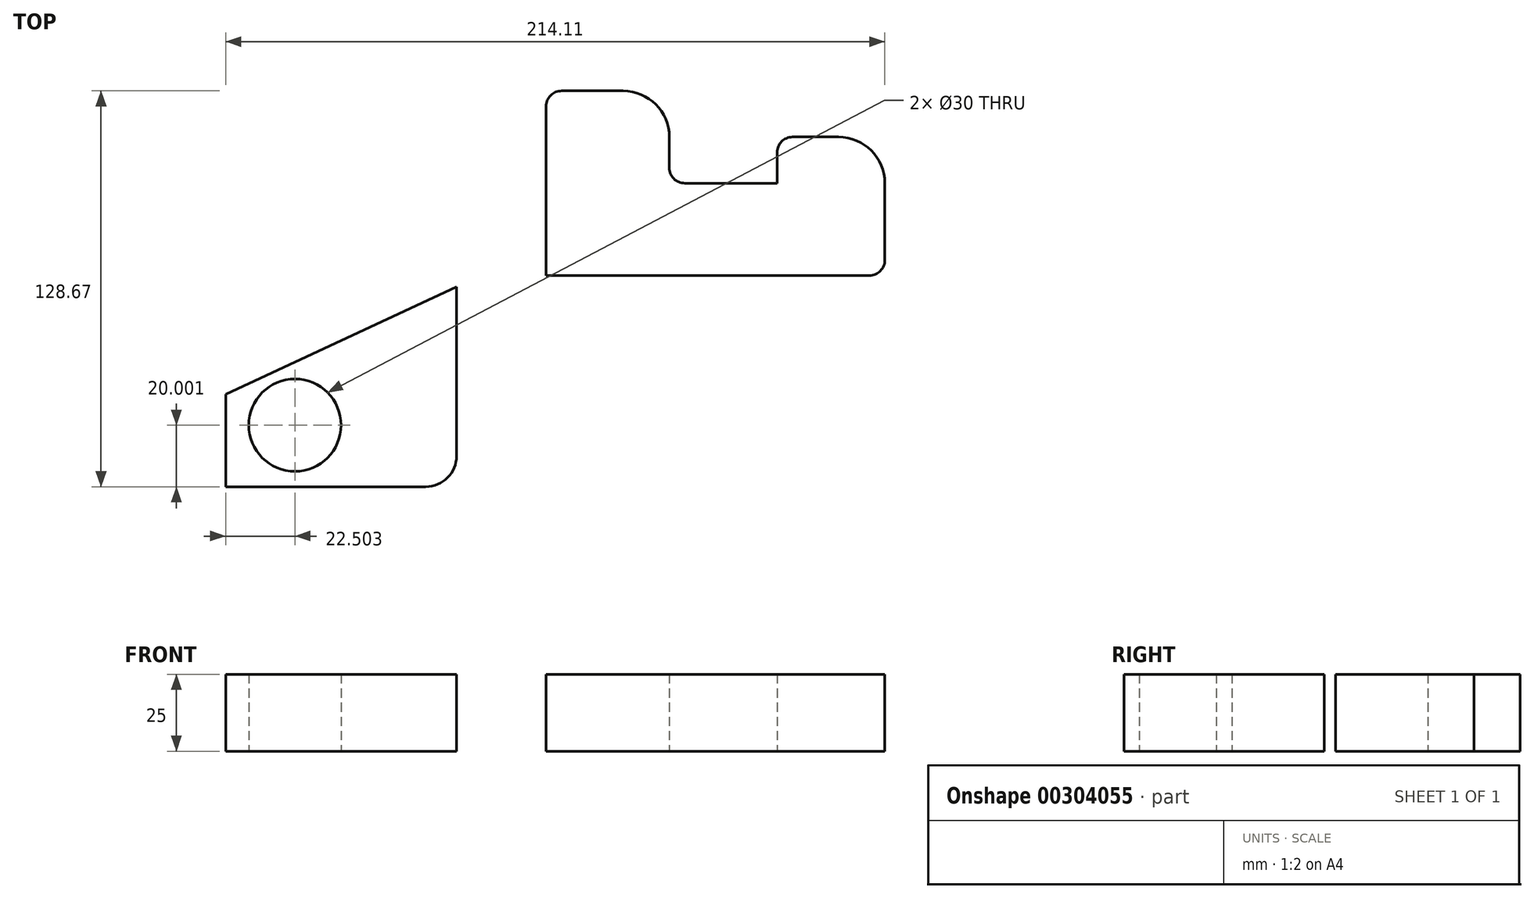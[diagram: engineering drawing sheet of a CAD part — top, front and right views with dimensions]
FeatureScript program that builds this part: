
annotation { "Feature Type Name" : "Feature", "Feature Type Description" : "" }
export const myFeature = defineFeature(function(context is Context, id is Id, definition is map)
    precondition{}
    {
        {
            var Q0;
            Q0=qCreatedBy(makeId("Top.planeOp"),FACE);
            var sketch = newSketch(context, id + "F0", { "sketchPlane" : qUnion([Q0])});
            skLineSegment(sketch, "E0", {"start": v(-72.12, -25.71) * mm, "end": v(32.88, -25.71) * mm});
            skLineSegment(sketch, "E1", {"start": v(37.88, -20.71) * mm, "end": v(37.88, 4.29) * mm});
            skPoint(sketch, "E2.visualSharp", {"position": v(37.88, -25.71) * mm});
            skArc(sketch, "E2.filletArc", {"start": v(32.88, -25.71) * mm, "mid": v(36.41, -24.25) * mm, "end": v(37.88, -20.71) * mm});
            skLineSegment(sketch, "E3", {"start": v(22.88, 19.29) * mm, "end": v(7.88, 19.29) * mm});
            skPoint(sketch, "E4.visualSharp", {"position": v(37.88, 19.29) * mm});
            skArc(sketch, "E4.filletArc", {"start": v(37.88, 4.29) * mm, "mid": v(33.48, 14.9) * mm, "end": v(22.88, 19.29) * mm});
            skLineSegment(sketch, "E5", {"start": v(2.88, 14.29) * mm, "end": v(2.88, 4.29) * mm});
            skPoint(sketch, "E6.visualSharp", {"position": v(2.88, 19.29) * mm});
            skArc(sketch, "E6.filletArc", {"start": v(7.88, 19.29) * mm, "mid": v(4.34, 17.82) * mm, "end": v(2.88, 14.29) * mm});
            skLineSegment(sketch, "E7", {"start": v(2.88, 4.29) * mm, "end": v(-27.12, 4.29) * mm});
            skLineSegment(sketch, "E8", {"start": v(-32.12, 9.29) * mm, "end": v(-32.12, 19.29) * mm});
            skPoint(sketch, "E9.visualSharp", {"position": v(-32.12, 4.29) * mm});
            skArc(sketch, "E9.filletArc", {"start": v(-32.12, 9.29) * mm, "mid": v(-30.66, 5.75) * mm, "end": v(-27.12, 4.29) * mm});
            skLineSegment(sketch, "E10", {"start": v(-47.12, 34.29) * mm, "end": v(-67.12, 34.29) * mm});
            skLineSegment(sketch, "E11", {"start": v(-72.12, 29.29) * mm, "end": v(-72.12, -25.71) * mm});
            skPoint(sketch, "E12.visualSharp", {"position": v(-72.12, 34.29) * mm});
            skArc(sketch, "E12.filletArc", {"start": v(-67.12, 34.29) * mm, "mid": v(-70.66, 32.82) * mm, "end": v(-72.12, 29.29) * mm});
            skPoint(sketch, "E13.visualSharp", {"position": v(-32.12, 34.29) * mm});
            skArc(sketch, "E13.filletArc", {"start": v(-32.12, 19.29) * mm, "mid": v(-36.52, 29.9) * mm, "end": v(-47.12, 34.29) * mm});
            skLineSegment(sketch, "E14", {"start": v(-176.23, -94.38) * mm, "end": v(-111.23, -94.38) * mm});
            skLineSegment(sketch, "E15", {"start": v(-101.23, -84.38) * mm, "end": v(-101.23, -29.38) * mm});
            skPoint(sketch, "E16.visualSharp", {"position": v(-101.23, -94.38) * mm});
            skArc(sketch, "E16.filletArc", {"start": v(-111.23, -94.38) * mm, "mid": v(-104.16, -91.45) * mm, "end": v(-101.23, -84.38) * mm});
            skLineSegment(sketch, "E17", {"start": v(-101.23, -29.38) * mm, "end": v(-176.23, -64.38) * mm});
            skCircle(sketch, "E18", {"center": v(-153.73, -74.38) * mm, "radius": 15 * mm});
            skLineSegment(sketch, "E19", {"start": v(-176.23, -64.38) * mm, "end": v(-176.23, -94.38) * mm});
            skSolve(sketch);
        }
        {
            var Q0;
            Q0 = qSketchRegion(id + "F0", true);
            extrude(context, id + "F1", {"entities" : qUnion([Q0]), "depth" : 25 * mm});
        }
        {
            var Q0;
            Q0 = qSketchRegion(id + "F0", true);
            extrude(context, id + "F2", {"entities" : qUnion([Q0]), "depth" : 25 * mm});
        }
    });
